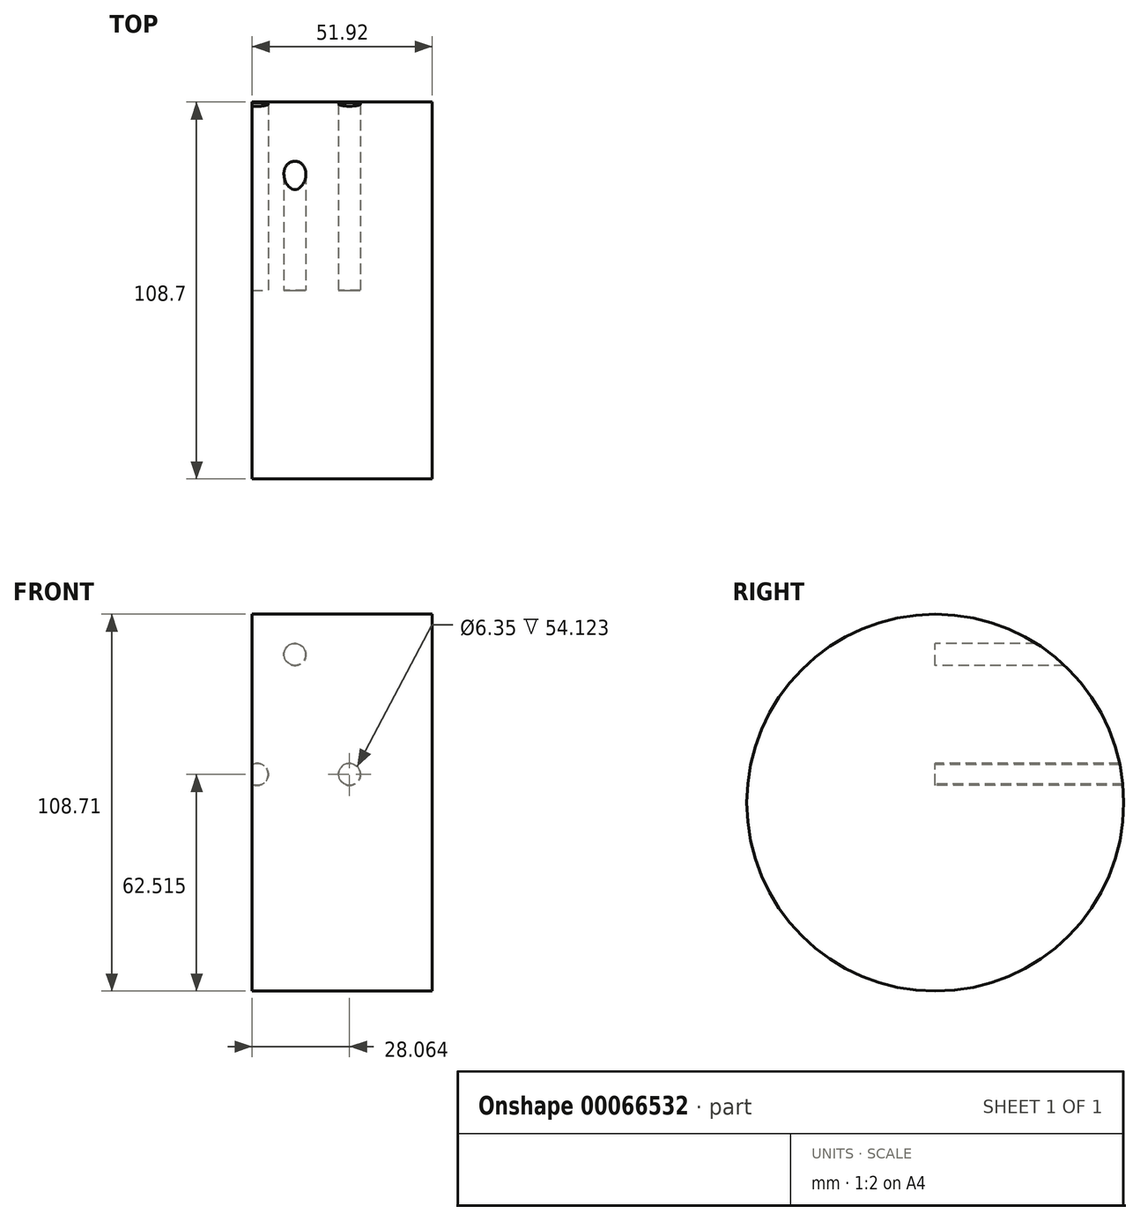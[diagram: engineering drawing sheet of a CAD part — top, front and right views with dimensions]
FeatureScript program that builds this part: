
annotation { "Feature Type Name" : "Feature", "Feature Type Description" : "" }
export const myFeature = defineFeature(function(context is Context, id is Id, definition is map)
    precondition{}
    {
        {
            var Q0;
            Q0=qCreatedBy(makeId("Front.planeOp"),FACE);
            var sketch = newSketch(context, id + "F0", { "sketchPlane" : qUnion([Q0])});
            skLineSegment(sketch, "E0", {"start": v(-39.47, 37.2) * mm, "end": v(12.45, 37.2) * mm});
            skLineSegment(sketch, "E1", {"start": v(12.45, 37.2) * mm, "end": v(12.45, -17.16) * mm});
            skLineSegment(sketch, "E2", {"start": v(12.45, -17.16) * mm, "end": v(-39.47, -17.16) * mm});
            skLineSegment(sketch, "E3", {"start": v(-39.47, -17.16) * mm, "end": v(-39.47, 37.2) * mm});
            skSolve(sketch);
        }
        {
            var Q0;
            Q0=makeQuery(id+"F0.imprint","IMPRINT",FACE,{"disambiguationData":[TD([[makeQuery(id+"F0.imprint","IMPRINT",EDGE,{"derivedFrom":sQuery(id+"F0.wireOp",EDGE,"E0")}),-1.0]])]});
            var Q1;
            Q1=sQuery(id+"F0.wireOp",EDGE,"E2");
            revolve(context, id + "F1", {"entities" : qUnion([Q0]), "axis" : qUnion([Q1]), "revolveType" : RevolveType.FULL});
        }
        {
            var Q0;
            Q0=qCreatedBy(makeId("Front.planeOp"),FACE);
            var sketch = newSketch(context, id + "F2", { "sketchPlane" : qUnion([Q0])});
            skPoint(sketch, "E4", {"position": v(-11.4, -9) * mm});
            skPoint(sketch, "E5", {"position": v(-38.02, -9) * mm});
            skPoint(sketch, "E6", {"position": v(-27.16, 25.56) * mm});
            skSolve(sketch);
        }
        {
            var Q0;
            Q0=sQuery(id+"F2.wireOp",VERTEX,"E6");
            var Q1;
            Q1=sQuery(id+"F2.wireOp",VERTEX,"E5");
            var Q2;
            Q2=sQuery(id+"F2.wireOp",VERTEX,"E4");
            var Q3;
            Q3=makeQuery(id+"F1.opRevolve","SWEPT_BODY",BODY,{"disambiguationData":[OSD([sQuery(id+"F0.wireOp",EDGE,"E0"),sQuery(id+"F0.wireOp",EDGE,"E1"),sQuery(id+"F0.wireOp",EDGE,"E2"),sQuery(id+"F0.wireOp",EDGE,"E3")])]});
            hole(context, id + "F3", {"style" : HoleStyle.SIMPLE, "holeDiameter" : 6.35 * mm, "endStyle" : HoleEndStyle.THROUGH, "locations" : qUnion([Q0, Q1, Q2]), "scope" : qUnion([Q3])});
        }
    });
